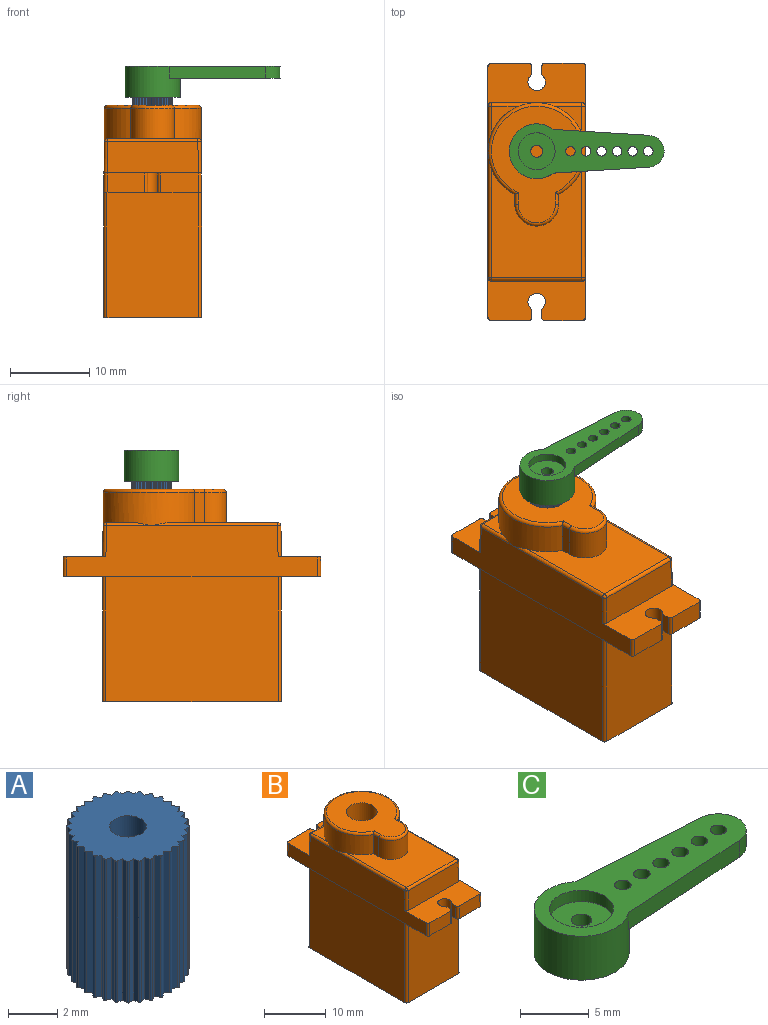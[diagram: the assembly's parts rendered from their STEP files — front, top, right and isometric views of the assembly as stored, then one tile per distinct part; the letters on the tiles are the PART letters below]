
ASSEMBLY  parts=3 mates=2
PART A: 99 faces, bbox 5x5x7.1 mm
  f0: plane 5x5mm, normal (0,0,-1), area 16.5mm2, adj f1,f2,f3,f4,f5,f6,f7,f8
  f1: plane 7.05x0.2mm, normal (-0.8,0.6,0), area 1.7mm2, adj f0,f2,f94,f95
  f2: cylinder r=0.08mm len=7.05mm, axis (0,0,-1), area 0.9mm2, adj f0,f1,f3,f94
  f3: plane 7.05x0.21mm, normal (-0.51,-0.86,0), area 1.7mm2, adj f0,f2,f4,f94
  f4: plane 7.05x0.22mm, normal (-0.9,0.43,0), area 1.7mm2, adj f0,f3,f5,f94
  f5: cylinder r=0.08mm len=7.05mm, axis (0,0,-1), area 0.9mm2, adj f0,f4,f6,f94
  f6: plane 7.05x0.23mm, normal (-0.33,-0.94,0), area 1.7mm2, adj f0,f5,f7,f94
  f7: plane 7.05x0.24mm, normal (-0.97,0.25,0), area 1.7mm2, adj f0,f6,f8,f94
  f8: cylinder r=0.08mm len=7.05mm, axis (0,0,-1), area 0.9mm2, adj f0,f7,f9,f94
  f9: plane 7.05x0.25mm, normal (-0.14,-0.99,0), area 1.7mm2, adj f0,f8,f10,f94
  f10: plane 7.05x0.25mm, normal (-1,0.05,0), area 1.7mm2, adj f0,f9,f11,f94
  f11: cylinder r=0.08mm len=7.05mm, axis (0,0,-1), area 0.9mm2, adj f0,f10,f12,f94
  f12: plane 7.05x0.25mm, normal (0.05,-1,0), area 1.7mm2, adj f0,f11,f13,f94
  f13: plane 7.05x0.25mm, normal (-0.99,-0.14,0), area 1.7mm2, adj f0,f12,f14,f94
  f14: cylinder r=0.08mm len=7.05mm, axis (0,0,-1), area 0.9mm2, adj f0,f13,f15,f94
  f15: plane 7.05x0.24mm, normal (0.25,-0.97,0), area 1.7mm2, adj f0,f14,f16,f94
  f16: plane 7.05x0.23mm, normal (-0.94,-0.33,0), area 1.7mm2, adj f0,f15,f17,f94
  f17: cylinder r=0.08mm len=7.05mm, axis (0,0,-1), area 0.9mm2, adj f0,f16,f18,f94
  f18: plane 7.05x0.22mm, normal (0.43,-0.9,0), area 1.7mm2, adj f0,f17,f19,f94
  f19: plane 7.05x0.21mm, normal (-0.86,-0.51,0), area 1.7mm2, adj f0,f18,f20,f94
  f20: cylinder r=0.08mm len=7.05mm, axis (0,0,-1), area 0.9mm2, adj f0,f19,f21,f94
  f21: plane 7.05x0.2mm, normal (0.6,-0.8,0), area 1.7mm2, adj f0,f20,f22,f94
  f22: plane 7.05x0.18mm, normal (-0.74,-0.67,0), area 1.7mm2, adj f0,f21,f23,f94
  f23: cylinder r=0.08mm len=7.05mm, axis (0,0,-1), area 0.9mm2, adj f0,f22,f24,f94
  f24: plane 7.05x0.18mm, normal (0.74,-0.67,0), area 1.7mm2, adj f0,f23,f25,f94
  f25: plane 7.05x0.2mm, normal (-0.6,-0.8,0), area 1.7mm2, adj f0,f24,f26,f94
  f26: cylinder r=0.08mm len=7.05mm, axis (0,0,-1), area 0.9mm2, adj f0,f25,f27,f94
  f27: plane 7.05x0.21mm, normal (0.86,-0.51,0), area 1.7mm2, adj f0,f26,f28,f94
  f28: plane 7.05x0.22mm, normal (-0.43,-0.9,0), area 1.7mm2, adj f0,f27,f29,f94
  f29: cylinder r=0.08mm len=7.05mm, axis (0,0,-1), area 0.9mm2, adj f0,f28,f30,f94
  f30: plane 7.05x0.23mm, normal (0.94,-0.33,0), area 1.7mm2, adj f0,f29,f31,f94
  f31: plane 7.05x0.24mm, normal (-0.25,-0.97,0), area 1.7mm2, adj f0,f30,f32,f94
  f32: cylinder r=0.08mm len=7.05mm, axis (0,0,-1), area 0.9mm2, adj f0,f31,f33,f94
  f33: plane 7.05x0.25mm, normal (0.99,-0.14,0), area 1.7mm2, adj f0,f32,f34,f94
  f34: plane 7.05x0.25mm, normal (-0.05,-1,0), area 1.7mm2, adj f0,f33,f35,f94
  f35: cylinder r=0.08mm len=7.05mm, axis (0,0,-1), area 0.9mm2, adj f0,f34,f36,f94
  f36: plane 7.05x0.25mm, normal (1,0.05,0), area 1.7mm2, adj f0,f35,f37,f94
  f37: plane 7.05x0.25mm, normal (0.14,-0.99,0), area 1.7mm2, adj f0,f36,f38,f94
  f38: cylinder r=0.08mm len=7.05mm, axis (0,0,-1), area 0.9mm2, adj f0,f37,f39,f94
  f39: plane 7.05x0.24mm, normal (0.97,0.25,0), area 1.7mm2, adj f0,f38,f40,f94
  f40: plane 7.05x0.23mm, normal (0.33,-0.94,0), area 1.7mm2, adj f0,f39,f41,f94
  f41: cylinder r=0.08mm len=7.05mm, axis (0,0,-1), area 0.9mm2, adj f0,f40,f42,f94
  f42: plane 7.05x0.22mm, normal (0.9,0.43,0), area 1.7mm2, adj f0,f41,f43,f94
  f43: plane 7.05x0.21mm, normal (0.51,-0.86,0), area 1.7mm2, adj f0,f42,f44,f94
  f44: cylinder r=0.08mm len=7.05mm, axis (0,0,-1), area 0.9mm2, adj f0,f43,f45,f94
  f45: plane 7.05x0.2mm, normal (0.8,0.6,0), area 1.7mm2, adj f0,f44,f46,f94
  f46: plane 7.05x0.18mm, normal (0.67,-0.74,0), area 1.7mm2, adj f0,f45,f47,f94
  f47: cylinder r=0.08mm len=7.05mm, axis (0,0,-1), area 0.9mm2, adj f0,f46,f48,f94
  f48: plane 7.05x0.18mm, normal (0.67,0.74,0), area 1.7mm2, adj f0,f47,f49,f94
  f49: plane 7.05x0.2mm, normal (0.8,-0.6,0), area 1.7mm2, adj f0,f48,f50,f94
  f50: cylinder r=0.08mm len=7.05mm, axis (0,0,-1), area 0.9mm2, adj f0,f49,f51,f94
  f51: plane 7.05x0.21mm, normal (0.51,0.86,0), area 1.7mm2, adj f0,f50,f52,f94
  f52: plane 7.05x0.22mm, normal (0.9,-0.43,0), area 1.7mm2, adj f0,f51,f53,f94
  f53: cylinder r=0.08mm len=7.05mm, axis (0,0,-1), area 0.9mm2, adj f0,f52,f54,f94
  f54: plane 7.05x0.23mm, normal (0.33,0.94,0), area 1.7mm2, adj f0,f53,f55,f94
  f55: plane 7.05x0.24mm, normal (0.97,-0.25,0), area 1.7mm2, adj f0,f54,f56,f94
  f56: cylinder r=0.08mm len=7.05mm, axis (0,0,-1), area 0.9mm2, adj f0,f55,f57,f94
  f57: plane 7.05x0.25mm, normal (0.14,0.99,0), area 1.7mm2, adj f0,f56,f58,f94
  f58: plane 7.05x0.25mm, normal (1,-0.05,0), area 1.7mm2, adj f0,f57,f59,f94
  f59: cylinder r=0.08mm len=7.05mm, axis (0,0,-1), area 0.9mm2, adj f0,f58,f60,f94
  f60: plane 7.05x0.25mm, normal (-0.05,1,0), area 1.7mm2, adj f0,f59,f61,f94
  f61: plane 7.05x0.25mm, normal (0.99,0.14,0), area 1.7mm2, adj f0,f60,f62,f94
  f62: cylinder r=0.08mm len=7.05mm, axis (0,0,-1), area 0.9mm2, adj f0,f61,f63,f94
  f63: plane 7.05x0.24mm, normal (-0.25,0.97,0), area 1.7mm2, adj f0,f62,f64,f94
  f64: plane 7.05x0.23mm, normal (0.94,0.33,0), area 1.7mm2, adj f0,f63,f65,f94
  f65: cylinder r=0.08mm len=7.05mm, axis (0,0,-1), area 0.9mm2, adj f0,f64,f66,f94
  f66: plane 7.05x0.22mm, normal (-0.43,0.9,0), area 1.7mm2, adj f0,f65,f67,f94
  f67: plane 7.05x0.21mm, normal (0.86,0.51,0), area 1.7mm2, adj f0,f66,f68,f94
  f68: cylinder r=0.08mm len=7.05mm, axis (0,0,-1), area 0.9mm2, adj f0,f67,f69,f94
  f69: plane 7.05x0.2mm, normal (-0.6,0.8,0), area 1.7mm2, adj f0,f68,f70,f94
  f70: plane 7.05x0.18mm, normal (0.74,0.67,0), area 1.7mm2, adj f0,f69,f71,f94
  f71: cylinder r=0.08mm len=7.05mm, axis (0,0,-1), area 0.9mm2, adj f0,f70,f72,f94
  f72: plane 7.05x0.18mm, normal (-0.74,0.67,0), area 1.7mm2, adj f0,f71,f73,f94
  f73: plane 7.05x0.2mm, normal (0.6,0.8,0), area 1.7mm2, adj f0,f72,f74,f94
  f74: cylinder r=0.08mm len=7.05mm, axis (0,0,-1), area 0.9mm2, adj f0,f73,f75,f94
  f75: plane 7.05x0.21mm, normal (-0.86,0.51,0), area 1.7mm2, adj f0,f74,f76,f94
  f76: plane 7.05x0.22mm, normal (0.43,0.9,0), area 1.7mm2, adj f0,f75,f77,f94
  f77: cylinder r=0.08mm len=7.05mm, axis (0,0,-1), area 0.9mm2, adj f0,f76,f78,f94
  f78: plane 7.05x0.23mm, normal (-0.94,0.33,0), area 1.7mm2, adj f0,f77,f79,f94
  f79: plane 7.05x0.24mm, normal (0.25,0.97,0), area 1.7mm2, adj f0,f78,f80,f94
  f80: cylinder r=0.08mm len=7.05mm, axis (0,0,-1), area 0.9mm2, adj f0,f79,f81,f94
  f81: plane 7.05x0.25mm, normal (-0.99,0.14,0), area 1.7mm2, adj f0,f80,f82,f94
  f82: plane 7.05x0.25mm, normal (0.05,1,0), area 1.7mm2, adj f0,f81,f83,f94
  f83: cylinder r=0.08mm len=7.05mm, axis (0,0,-1), area 0.9mm2, adj f0,f82,f84,f94
  f84: plane 7.05x0.25mm, normal (-1,-0.05,0), area 1.7mm2, adj f0,f83,f85,f94
  f85: plane 7.05x0.25mm, normal (-0.14,0.99,0), area 1.7mm2, adj f0,f84,f86,f94
  f86: cylinder r=0.08mm len=7.05mm, axis (0,0,-1), area 0.9mm2, adj f0,f85,f87,f94
  f87: plane 7.05x0.24mm, normal (-0.97,-0.25,0), area 1.7mm2, adj f0,f86,f88,f94
  f88: plane 7.05x0.23mm, normal (-0.33,0.94,0), area 1.7mm2, adj f0,f87,f89,f94
  f89: cylinder r=0.08mm len=7.05mm, axis (0,0,-1), area 0.9mm2, adj f0,f88,f90,f94
  f90: plane 7.05x0.22mm, normal (-0.9,-0.43,0), area 1.7mm2, adj f0,f89,f91,f94
  f91: plane 7.05x0.21mm, normal (-0.51,0.86,0), area 1.7mm2, adj f0,f90,f92,f94
  f92: cylinder r=0.08mm len=7.05mm, axis (0,0,-1), area 0.9mm2, adj f0,f91,f93,f94
  f93: plane 7.05x0.2mm, normal (-0.8,-0.6,0), area 1.7mm2, adj f0,f92,f94,f96
  f94: plane 5x5mm, normal (0,0,1), area 16.5mm2, adj f1,f2,f3,f4,f5,f6,f7,f8
  f95: plane 7.05x0.18mm, normal (-0.67,-0.74,0), area 1.7mm2, adj f0,f1,f94,f97
  f96: plane 7.05x0.18mm, normal (-0.67,0.74,0), area 1.7mm2, adj f0,f93,f94,f97
  f97: cylinder r=0.08mm len=7.05mm, axis (0,0,-1), area 0.9mm2, adj f0,f94,f95,f96
  f98: cylinder r=0.75mm len=7.05mm, axis (0,0,-1), area 33.2mm2, adj f0,f94
PART B: 64 faces, bbox 13.2x32.4x26.7 mm
  f0: plane 3.52x3.52mm, normal (0,0,1), area 4.4mm2, adj f4,f7,f57
  f1: plane 3.52x3.52mm, normal (0,0,1), area 4.4mm2, adj f5,f8,f57
  f2: plane 13.72x11.39mm, normal (0,0,1), area 107.7mm2, adj f3,f6,f47,f53,f54,f57,f58
  f3: cylinder r=0.4mm len=15.89mm, axis (0,1,0), area 9.3mm2, adj f2,f17,f45,f57
  f4: cylinder r=0.4mm len=5.69mm, axis (0,1,0), area 2.9mm2, adj f0,f17,f50,f57
  f5: cylinder r=0.4mm len=5.69mm, axis (0,1,0), area 2.9mm2, adj f1,f15,f51,f57
  f6: cylinder r=0.4mm len=15.89mm, axis (0,1,0), area 9.3mm2, adj f2,f15,f49,f57
  f7: cylinder r=0.4mm len=5.69mm, axis (-1,0,0), area 2.9mm2, adj f0,f16,f50,f57
  f8: cylinder r=0.4mm len=5.69mm, axis (-1,0,0), area 2.9mm2, adj f1,f16,f51,f57
  f9: plane 4.73x2.5mm, normal (0,1,0.01), area 11.8mm2, adj f11,f12,f32,f36
  f10: plane 4.73x2.5mm, normal (0,1,0.01), area 11.8mm2, adj f11,f12,f33,f37
  f11: plane 12.3x5.35mm, normal (0,0,-1), area 55.4mm2, adj f9,f10,f15,f17,f22,f29,f30,f31
  f12: plane 12.26x5.35mm, normal (0,0,1), area 55.2mm2, adj f9,f10,f15,f16,f17,f29,f30,f31
  f13: plane 4.73x2.5mm, normal (0,-1,0.01), area 11.8mm2, adj f14,f25,f34,f38
  f14: plane 12.26x5.35mm, normal (0,0,1), area 55.2mm2, adj f13,f15,f17,f18,f24,f26,f27,f28
  f15: plane 31.6x6.4mm, normal (1,0,0.01), area 163.4mm2, adj f5,f6,f11,f12,f14,f23,f25,f36
  f16: plane 11.46x3.9mm, normal (0,1,0.01), area 44.6mm2, adj f7,f8,f12,f48,f52
  f17: plane 31.6x6.4mm, normal (-1,0,0.01), area 163.4mm2, adj f3,f4,f11,f12,f14,f21,f25,f37
  f18: plane 11.46x3.9mm, normal (0,-1,0.01), area 44.6mm2, adj f14,f44,f46,f47
  f19: plane 22.5x12.3mm, normal (0,0,-1), area 276.6mm2, adj f20,f21,f22,f23,f40,f41,f42,f43
  f20: plane 15.7x11.5mm, normal (0,-1,0), area 180.5mm2, adj f19,f25,f42,f43
  f21: plane 21.7x15.7mm, normal (-1,0,0), area 340.7mm2, adj f17,f19,f41,f42
  f22: plane 15.7x11.5mm, normal (0,1,0), area 180.5mm2, adj f11,f19,f40,f41
  f23: plane 21.7x15.7mm, normal (1,0,0), area 340.7mm2, adj f15,f19,f40,f43
  f24: plane 4.73x2.5mm, normal (0,-1,0.01), area 11.8mm2, adj f14,f25,f35,f39
  f25: plane 12.3x5.35mm, normal (0,0,-1), area 55.4mm2, adj f13,f15,f17,f20,f24,f26,f27,f28
  f26: cylinder r=1.1mm len=2.5mm, axis (0,0,1), area 14mm2, adj f14,f25,f27,f28
  f27: plane 2.5x1.04mm, normal (1,0,0), area 2.6mm2, adj f14,f25,f26,f34
  f28: plane 2.5x1.04mm, normal (-1,0,0), area 2.6mm2, adj f14,f25,f26,f35
  f29: plane 2.5x1.04mm, normal (-1,0,0), area 2.6mm2, adj f11,f12,f31,f32
  f30: plane 2.5x1.04mm, normal (1,0,0), area 2.6mm2, adj f11,f12,f31,f33
  f31: cylinder r=1.1mm len=2.5mm, axis (0,0,1), area 14mm2, adj f11,f12,f29,f30
  f32: cylinder r=0.4mm len=2.51mm, axis (0,0.01,-1), area 1.6mm2, adj f9,f11,f12,f29
  f33: cylinder r=0.4mm len=2.51mm, axis (0,-0.01,1), area 1.6mm2, adj f10,f11,f12,f30
  f34: cylinder r=0.4mm len=2.51mm, axis (0,0.01,1), area 1.6mm2, adj f13,f14,f25,f27
  f35: cylinder r=0.4mm len=2.51mm, axis (0,-0.01,-1), area 1.6mm2, adj f14,f24,f25,f28
  f36: cylinder r=0.4mm len=2.5mm, axis (0.01,0.01,-1), area 1.6mm2, adj f9,f11,f12,f15
  f37: cylinder r=0.4mm len=2.5mm, axis (-0.01,0.01,-1), area 1.6mm2, adj f10,f11,f12,f17
  f38: cylinder r=0.4mm len=2.5mm, axis (-0.01,-0.01,-1), area 1.6mm2, adj f13,f14,f17,f25
  f39: cylinder r=0.4mm len=2.5mm, axis (0.01,-0.01,-1), area 1.6mm2, adj f14,f15,f24,f25
  f40: cylinder r=0.4mm len=15.7mm, axis (0,0,-1), area 9.9mm2, adj f11,f19,f22,f23
  f41: cylinder r=0.4mm len=15.7mm, axis (0,0,1), area 9.9mm2, adj f11,f19,f21,f22
  f42: cylinder r=0.4mm len=15.7mm, axis (0,0,-1), area 9.9mm2, adj f19,f20,f21,f25
  f43: cylinder r=0.4mm len=15.7mm, axis (0,0,1), area 9.9mm2, adj f19,f20,f23,f25
  f44: cylinder r=0.4mm len=3.91mm, axis (-0.01,-0.01,-1), area 2.5mm2, adj f14,f17,f18,f45
  f45: sphere r=0.4mm, area 0.2mm2, adj f3,f44,f47
  f46: cylinder r=0.4mm len=3.91mm, axis (0.01,-0.01,-1), area 2.5mm2, adj f14,f15,f18,f49
  f47: cylinder r=0.4mm len=11.39mm, axis (-1,0,0), area 7.1mm2, adj f2,f18,f45,f49
  f48: cylinder r=0.4mm len=3.91mm, axis (-0.01,0.01,-1), area 2.5mm2, adj f12,f16,f17,f50
  f49: sphere r=0.4mm, area 0.2mm2, adj f6,f46,f47
  f50: sphere r=0.4mm, area 0.2mm2, adj f4,f7,f48
  f51: sphere r=0.4mm, area 0.2mm2, adj f5,f8,f52
  f52: cylinder r=0.4mm len=3.91mm, axis (0.01,0.01,-1), area 2.5mm2, adj f12,f15,f16,f51
  f53: plane 3.8x1.22mm, normal (-1,0,0), area 4.6mm2, adj f2,f54,f57,f61
  f54: cylinder r=2.75mm len=5.5mm, axis (0,0,-1), area 32.8mm2, adj f2,f53,f58,f63
  f55: plane 14.7x11.39mm, normal (0,0,1), area 96.2mm2, adj f56,f60,f61,f62,f63
  f56: cylinder r=2.5mm len=5mm, axis (0,0,-1), area 66mm2, adj f55,f59
  f57: cylinder r=6.09mm len=12.19mm, axis (0,0,-1), area 125.9mm2, adj f0,f1,f2,f3,f4,f5,f6,f7
  f58: plane 3.8x1.22mm, normal (1,0,0), area 4.6mm2, adj f2,f54,f57,f62
  f59: plane 5x5mm, normal (0,0,1), area 19.6mm2, adj f56
  f60: torus R=5.69mm, axis (0,0,1), area 20.1mm2, adj f55,f57,f61,f62
  f61: cylinder r=0.4mm len=1.47mm, axis (0,1,0), area 0.8mm2, adj f53,f55,f60,f63
  f62: cylinder r=0.4mm len=1.47mm, axis (0,-1,0), area 0.8mm2, adj f55,f58,f60,f63
  f63: torus R=2.35mm, axis (0,0,1), area 5.1mm2, adj f54,f55,f61,f62
PART C: 18 faces, bbox 19.5x6.9x3.9 mm
  f0: plane 4.65x4.65mm, normal (0,0,1), area 15.2mm2, adj f1,f7
  f1: cylinder r=0.75mm len=1.5mm, axis (0,0,-1), area 4.9mm2, adj f0,f2
  f2: plane 5x5mm, normal (0,0,-1), area 17.9mm2, adj f1,f3
  f3: cylinder r=2.5mm len=5mm, axis (0,0,-1), area 29.1mm2, adj f2,f4
  f4: plane 6.9x6.9mm, normal (0,0,-1), area 17.8mm2, adj f3,f5
  f5: cylinder r=3.45mm len=6.9mm, axis (0,0,-1), area 75mm2, adj f4,f6,f8,f9,f11
  f6: plane 19.5x6.9mm, normal (0,0,1), area 71.6mm2, adj f5,f7,f8,f9,f10,f12,f13,f14
  f7: cylinder r=2.32mm len=4.65mm, axis (0,0,-1), area 14.6mm2, adj f0,f6
  f8: plane 12.09x1.5mm, normal (0.06,1,0), area 18.2mm2, adj f5,f6,f10,f11
  f9: plane 12.09x1.5mm, normal (0.06,-1,0), area 18.2mm2, adj f5,f6,f10,f11
  f10: cylinder r=2mm len=4mm, axis (0,0,1), area 9.1mm2, adj f6,f8,f9,f11
  f11: plane 13.97x5.5mm, normal (0,0,-1), area 51.2mm2, adj f5,f8,f9,f10,f12,f13,f14,f15
  f12: cylinder r=0.6mm len=1.5mm, axis (0,0,1), area 5.7mm2, adj f6,f11
  f13: cylinder r=0.6mm len=1.5mm, axis (0,0,1), area 5.7mm2, adj f6,f11
  f14: cylinder r=0.6mm len=1.5mm, axis (0,0,1), area 5.7mm2, adj f6,f11
  f15: cylinder r=0.6mm len=1.5mm, axis (0,0,1), area 5.7mm2, adj f6,f11
  f16: cylinder r=0.6mm len=1.5mm, axis (0,0,1), area 5.7mm2, adj f6,f11
  f17: cylinder r=0.6mm len=1.5mm, axis (0,0,1), area 5.7mm2, adj f6,f11
PLACE A at identity
PLACE B at identity fixed
PLACE C at identity
MATE revolute B.f56 <-> A.f98  axis (0,0,-1) through (0,5.1,6.8)mm
MATE fastened C.f1 <-> A.f98  axis (0,0,-1) through (0,5.1,13.85)mm
